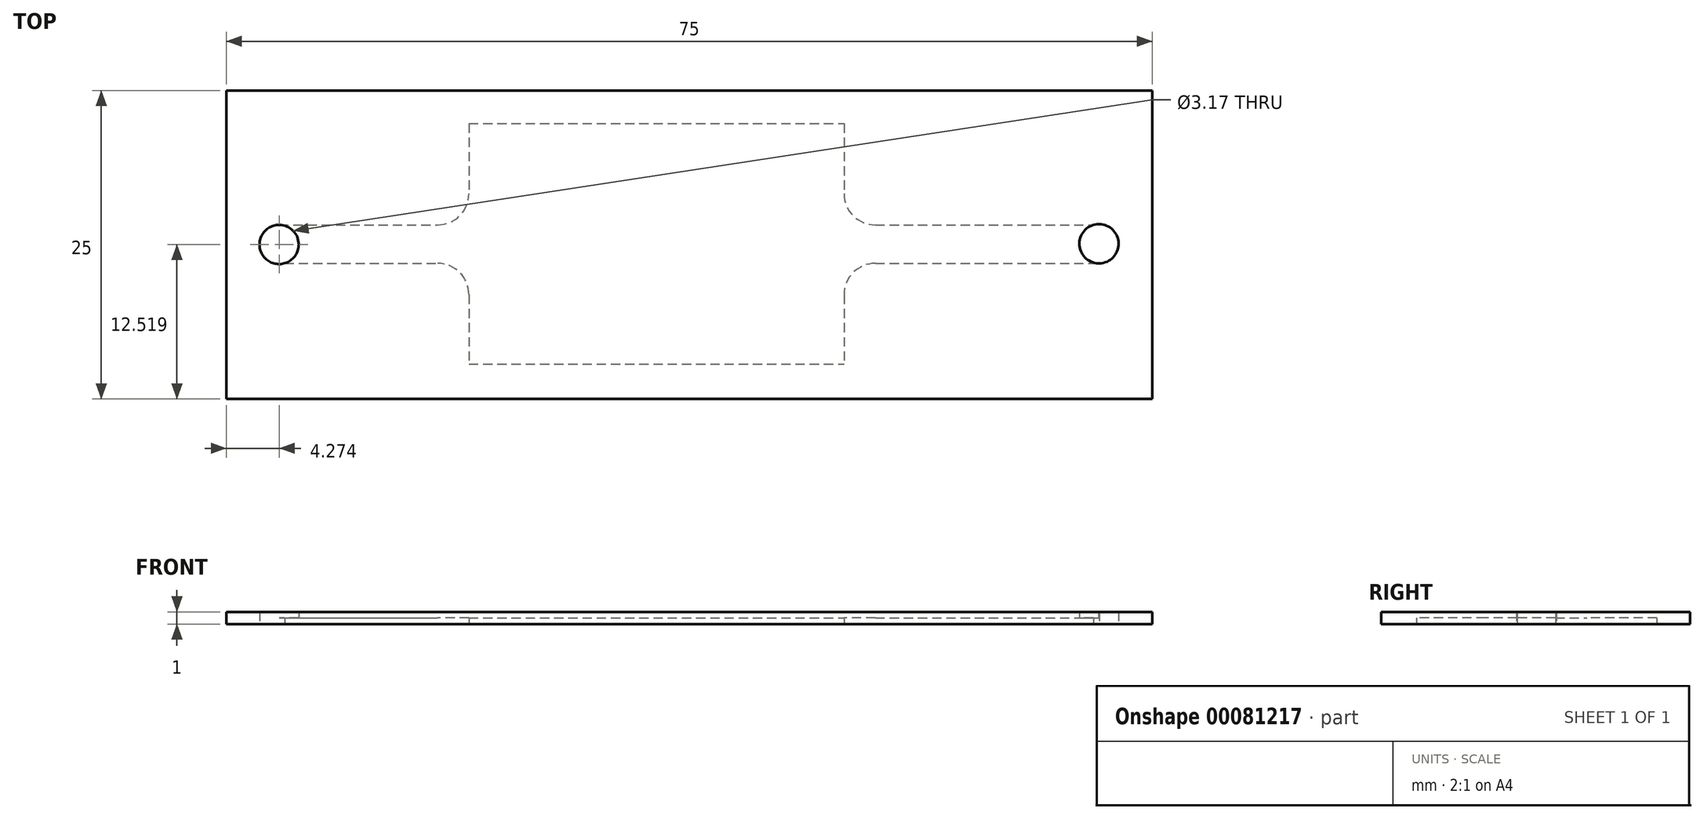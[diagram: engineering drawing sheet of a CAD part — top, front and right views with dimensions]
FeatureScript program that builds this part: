
annotation { "Feature Type Name" : "Feature", "Feature Type Description" : "" }
export const myFeature = defineFeature(function(context is Context, id is Id, definition is map)
    precondition{}
    {
        {
            var Q0;
            Q0=qCreatedBy(makeId("Top.planeOp"),FACE);
            var sketch = newSketch(context, id + "F0", { "sketchPlane" : qUnion([Q0])});
            skLineSegment(sketch, "E0.bottom", {"start": v(40.16, -6.83) * mm, "end": v(-34.84, -6.83) * mm});
            skLineSegment(sketch, "E0.top", {"start": v(40.16, 18.17) * mm, "end": v(-34.84, 18.17) * mm});
            skLineSegment(sketch, "E0.left", {"start": v(40.16, -6.83) * mm, "end": v(40.16, 18.17) * mm});
            skLineSegment(sketch, "E0.right", {"start": v(-34.84, -6.83) * mm, "end": v(-34.84, 18.17) * mm});
            skLineSegment(sketch, "E1", {"start": v(-34.84, -6.83) * mm, "end": v(-34.84, 5.67) * mm});
            skLineSegment(sketch, "E2", {"start": v(-34.84, 5.67) * mm, "end": v(40.16, 5.67) * mm});
            skSolve(sketch);
        }
        {
            var Q0;
            Q0=makeQuery(id+"F0.imprint","IMPRINT",FACE,{"disambiguationData":[TD([[makeQuery(id+"F0.imprint","IMPRINT",EDGE,{"derivedFrom":sQuery(id+"F0.wireOp",EDGE,"E0.bottom")}),-1.0]])]});
            var sketch = newSketch(context, id + "F1", { "sketchPlane" : qUnion([Q0])});
            skCircle(sketch, "E3", {"center": v(35.84, 5.75) * mm, "radius": 1.59 * mm});
            skCircle(sketch, "E4", {"center": v(-30.57, 5.69) * mm, "radius": 1.59 * mm});
            skLineSegment(sketch, "E5.bottom", {"start": v(-30.56, 7.28) * mm, "end": v(35.88, 7.28) * mm});
            skLineSegment(sketch, "E5.top", {"start": v(-30.56, 4.16) * mm, "end": v(35.88, 4.16) * mm});
            skLineSegment(sketch, "E5.left", {"start": v(-30.56, 7.28) * mm, "end": v(-30.56, 4.16) * mm});
            skLineSegment(sketch, "E5.right", {"start": v(35.88, 7.28) * mm, "end": v(35.88, 4.16) * mm});
            skLineSegment(sketch, "E6.bottom", {"start": v(-15.2, 15.49) * mm, "end": v(15.2, 15.49) * mm});
            skLineSegment(sketch, "E6.top", {"start": v(-15.2, -3.99) * mm, "end": v(15.2, -3.99) * mm});
            skLineSegment(sketch, "E6.left", {"start": v(-15.2, 15.49) * mm, "end": v(-15.2, -3.99) * mm});
            skLineSegment(sketch, "E6.right", {"start": v(15.2, 15.49) * mm, "end": v(15.2, -3.99) * mm});
            skPoint(sketch, "E6.middle", {"position": v(0, 5.75) * mm});
            skSolve(sketch);
        }
        {
            var Q0;
            {var subQ0=sQuery(id+"F0.wireOp",EDGE,"E0.bottom");Q0=makeQuery(id+"F0.imprint","IMPRINT",FACE,{"disambiguationData":[TD([[makeQuery(id+"F0.imprint","IMPRINT",EDGE,{"derivedFrom":subQ0}),-1.0]])]});}
            var Q1;
            {var subQ0=sQuery(id+"F0.wireOp",EDGE,"E0.top");Q1=makeQuery(id+"F0.imprint","IMPRINT",FACE,{"disambiguationData":[TD([[makeQuery(id+"F0.imprint","IMPRINT",EDGE,{"derivedFrom":subQ0}),1.0]])]});}
            extrude(context, id + "F2", {"entities" : qUnion([Q0, Q1]), "offsetDistance" : 25.4 * mm, "depth" : 1 * mm});
        }
        {
            var Q0;
            {var subQ1=sQuery(id+"F1.wireOp",EDGE,"E4");var subQ3=makeQuery(id+"F0.imprint","IMPRINT",EDGE,{"derivedFrom":sQuery(id+"F0.wireOp",EDGE,"E2")});var subQ4=makeQuery(id+"F1.imprint","INTERSECT",VERTEX,{"disambiguationData":[OD(0.0)],"derivedFrom":[subQ3,subQ1]});Q0=makeQuery(id+"F1.imprint","IMPRINT",FACE,{"disambiguationData":[TD([[makeQuery(id+"F1.imprint","IMPRINT",EDGE,{"disambiguationData":[TD([[subQ4,-1.0]])],"derivedFrom":subQ3}),1.0]])]});}
            var Q1;
            {var subQ0=sQuery(id+"F1.wireOp",EDGE,"E5.top");var subQ1=sQuery(id+"F1.wireOp",EDGE,"E4");var subQ2=makeQuery(id+"F1.imprint","INTERSECT",VERTEX,{"derivedFrom":[subQ1,subQ0]});Q1=makeQuery(id+"F1.imprint","IMPRINT",FACE,{"disambiguationData":[TD([[makeQuery(id+"F1.imprint","IMPRINT",EDGE,{"disambiguationData":[TD([[subQ2,1.0]])],"derivedFrom":subQ1}),1.0]])]});}
            var Q2;
            {var subQ0=sQuery(id+"F1.wireOp",EDGE,"E5.top");var subQ1=sQuery(id+"F1.wireOp",EDGE,"E4");var subQ2=makeQuery(id+"F1.imprint","INTERSECT",VERTEX,{"derivedFrom":[subQ1,subQ0]});Q2=makeQuery(id+"F1.imprint","IMPRINT",FACE,{"disambiguationData":[TD([[makeQuery(id+"F1.imprint","IMPRINT",EDGE,{"disambiguationData":[TD([[subQ2,-1.0]])],"derivedFrom":subQ1}),1.0]])]});}
            var Q3;
            {var subQ0=sQuery(id+"F1.wireOp",EDGE,"e85cab8e-166c-4b5d-8382-3d215b1240e5");var subQ1=sQuery(id+"F1.wireOp",EDGE,"E4");var subQ2=makeQuery(id+"F1.imprint","INTERSECT",VERTEX,{"derivedFrom":[subQ1,subQ0]});Q3=makeQuery(id+"F1.imprint","IMPRINT",FACE,{"disambiguationData":[TD([[makeQuery(id+"F1.imprint","IMPRINT",EDGE,{"disambiguationData":[TD([[subQ2,1.0]])],"derivedFrom":subQ1}),1.0]])]});}
            var Q4;
            {var subQ0=sQuery(id+"F1.wireOp",EDGE,"E5.bottom");var subQ1=sQuery(id+"F1.wireOp",EDGE,"E3");var subQ2=makeQuery(id+"F1.imprint","INTERSECT",VERTEX,{"derivedFrom":[subQ1,subQ0]});Q4=makeQuery(id+"F1.imprint","IMPRINT",FACE,{"disambiguationData":[TD([[makeQuery(id+"F1.imprint","IMPRINT",EDGE,{"disambiguationData":[TD([[subQ2,-1.0]])],"derivedFrom":subQ1}),1.0]])]});}
            var Q5;
            {var subQ0=sQuery(id+"F1.wireOp",EDGE,"E5.top");var subQ1=sQuery(id+"F1.wireOp",EDGE,"E3");var subQ2=makeQuery(id+"F1.imprint","INTERSECT",VERTEX,{"derivedFrom":[subQ1,subQ0]});Q5=makeQuery(id+"F1.imprint","IMPRINT",FACE,{"disambiguationData":[TD([[makeQuery(id+"F1.imprint","IMPRINT",EDGE,{"disambiguationData":[TD([[subQ2,1.0]])],"derivedFrom":subQ1}),1.0]])]});}
            var Q6;
            {var subQ1=sQuery(id+"F1.wireOp",EDGE,"E3");var subQ3=makeQuery(id+"F0.imprint","IMPRINT",EDGE,{"derivedFrom":sQuery(id+"F0.wireOp",EDGE,"E2")});var subQ4=makeQuery(id+"F1.imprint","INTERSECT",VERTEX,{"disambiguationData":[OD(0.0)],"derivedFrom":[subQ3,subQ1]});Q6=makeQuery(id+"F1.imprint","IMPRINT",FACE,{"disambiguationData":[TD([[makeQuery(id+"F1.imprint","IMPRINT",EDGE,{"disambiguationData":[TD([[subQ4,1.0]])],"derivedFrom":subQ3}),-1.0]])]});}
            var Q7;
            {var subQ0=sQuery(id+"F1.wireOp",EDGE,"E5.bottom");var subQ1=sQuery(id+"F1.wireOp",EDGE,"E3");var subQ2=makeQuery(id+"F1.imprint","INTERSECT",VERTEX,{"derivedFrom":[subQ1,subQ0]});Q7=makeQuery(id+"F1.imprint","IMPRINT",FACE,{"disambiguationData":[TD([[makeQuery(id+"F1.imprint","IMPRINT",EDGE,{"disambiguationData":[TD([[subQ2,1.0]])],"derivedFrom":subQ1}),1.0]])]});}
            var Q8;
            {var subQ1=sQuery(id+"F1.wireOp",EDGE,"E4");var subQ3=makeQuery(id+"F0.imprint","IMPRINT",EDGE,{"derivedFrom":sQuery(id+"F0.wireOp",EDGE,"E2")});var subQ4=makeQuery(id+"F1.imprint","INTERSECT",VERTEX,{"disambiguationData":[OD(1.0)],"derivedFrom":[subQ3,subQ1]});Q8=makeQuery(id+"F1.imprint","IMPRINT",FACE,{"disambiguationData":[TD([[makeQuery(id+"F1.imprint","IMPRINT",EDGE,{"disambiguationData":[TD([[subQ4,1.0]])],"derivedFrom":subQ3}),1.0]])]});}
            extrude(context, id + "F3", {"entities" : qUnion([Q0, Q1, Q2, Q3, Q4, Q5, Q6, Q7, Q8]), "operationType" : NewBodyOperationType.REMOVE, "depth" : 25.4 * mm});
        }
        {
            var Q0;
            {var subQ1=sQuery(id+"F1.wireOp",EDGE,"E5.top");var subQ8=sQuery(id+"F1.wireOp",EDGE,"E4");var subQ9=makeQuery(id+"F1.imprint","INTERSECT",VERTEX,{"derivedFrom":[subQ8,subQ1]});Q0=makeQuery(id+"F1.imprint","IMPRINT",FACE,{"disambiguationData":[TD([[makeQuery(id+"F1.imprint","IMPRINT",EDGE,{"disambiguationData":[TD([[subQ9,-1.0]])],"derivedFrom":subQ8}),-1.0]])]});}
            var Q1;
            {var subQ0=sQuery(id+"F1.wireOp",EDGE,"e85cab8e-166c-4b5d-8382-3d215b1240e5");var subQ3=sQuery(id+"F1.wireOp",EDGE,"E4");var subQ4=makeQuery(id+"F1.imprint","INTERSECT",VERTEX,{"derivedFrom":[subQ3,subQ0]});Q1=makeQuery(id+"F1.imprint","IMPRINT",FACE,{"disambiguationData":[TD([[makeQuery(id+"F1.imprint","IMPRINT",EDGE,{"disambiguationData":[TD([[subQ4,1.0]])],"derivedFrom":subQ3}),-1.0]])]});}
            var Q2;
            {var subQ5=sQuery(id+"F1.wireOp",EDGE,"E6.top");Q2=makeQuery(id+"F1.imprint","IMPRINT",FACE,{"disambiguationData":[TD([[makeQuery(id+"F1.imprint","IMPRINT",EDGE,{"derivedFrom":subQ5}),1.0]])]});}
            var Q3;
            {var subQ5=sQuery(id+"F1.wireOp",EDGE,"E6.bottom");Q3=makeQuery(id+"F1.imprint","IMPRINT",FACE,{"disambiguationData":[TD([[makeQuery(id+"F1.imprint","IMPRINT",EDGE,{"derivedFrom":subQ5}),-1.0]])]});}
            var Q4;
            {var subQ1=sQuery(id+"F1.wireOp",EDGE,"E5.bottom");var subQ7=sQuery(id+"F1.wireOp",EDGE,"E3");var subQ8=makeQuery(id+"F1.imprint","INTERSECT",VERTEX,{"derivedFrom":[subQ7,subQ1]});Q4=makeQuery(id+"F1.imprint","IMPRINT",FACE,{"disambiguationData":[TD([[makeQuery(id+"F1.imprint","IMPRINT",EDGE,{"disambiguationData":[TD([[subQ8,-1.0]])],"derivedFrom":subQ7}),-1.0]])]});}
            var Q5;
            {var subQ1=sQuery(id+"F1.wireOp",EDGE,"E5.top");var subQ3=sQuery(id+"F1.wireOp",EDGE,"E3");var subQ4=makeQuery(id+"F1.imprint","INTERSECT",VERTEX,{"derivedFrom":[subQ3,subQ1]});Q5=makeQuery(id+"F1.imprint","IMPRINT",FACE,{"disambiguationData":[TD([[makeQuery(id+"F1.imprint","IMPRINT",EDGE,{"disambiguationData":[TD([[subQ4,1.0]])],"derivedFrom":subQ3}),-1.0]])]});}
            var Q6;
            {var subQ0=sQuery(id+"F1.wireOp",EDGE,"E6.left");var subQ1=sQuery(id+"F1.wireOp",EDGE,"E5.bottom");var subQ2=makeQuery(id+"F1.imprint","INTERSECT",VERTEX,{"derivedFrom":[subQ1,subQ0]});Q6=makeQuery(id+"F1.imprint","IMPRINT",FACE,{"disambiguationData":[TD([[makeQuery(id+"F1.imprint","IMPRINT",EDGE,{"disambiguationData":[TD([[subQ2,-1.0]])],"derivedFrom":subQ1}),-1.0]])]});}
            var Q7;
            {var subQ0=sQuery(id+"F1.wireOp",EDGE,"E6.left");var subQ1=sQuery(id+"F1.wireOp",EDGE,"E5.top");var subQ2=makeQuery(id+"F1.imprint","INTERSECT",VERTEX,{"derivedFrom":[subQ1,subQ0]});Q7=makeQuery(id+"F1.imprint","IMPRINT",FACE,{"disambiguationData":[TD([[makeQuery(id+"F1.imprint","IMPRINT",EDGE,{"disambiguationData":[TD([[subQ2,-1.0]])],"derivedFrom":subQ1}),1.0]])]});}
            var Q8;
            {var subQ0=sQuery(id+"F1.wireOp",EDGE,"f7442fb1-22eb-4b81-94ff-7a8b5c8a4ed30.MirrorCS");var subQ1=sQuery(id+"F1.wireOp",EDGE,"E5.top");var subQ2=makeQuery(id+"F1.imprint","INTERSECT",VERTEX,{"disambiguationData":[OD(0.0)],"derivedFrom":[subQ1,subQ0]});Q8=makeQuery(id+"F1.imprint","IMPRINT",FACE,{"disambiguationData":[TD([[makeQuery(id+"F1.imprint","IMPRINT",EDGE,{"disambiguationData":[TD([[subQ2,-1.0]])],"derivedFrom":subQ1}),1.0]])]});}
            var Q9;
            {var subQ0=sQuery(id+"F1.wireOp",EDGE,"9eba685b-acd6-4631-9a7d-23c258058f2e0.MirrorCS");var subQ1=sQuery(id+"F1.wireOp",EDGE,"E5.top");var subQ2=makeQuery(id+"F1.imprint","INTERSECT",VERTEX,{"disambiguationData":[OD(0.0)],"derivedFrom":[subQ1,subQ0]});Q9=makeQuery(id+"F1.imprint","IMPRINT",FACE,{"disambiguationData":[TD([[makeQuery(id+"F1.imprint","IMPRINT",EDGE,{"disambiguationData":[TD([[subQ2,-1.0]])],"derivedFrom":subQ1}),1.0]])]});}
            var Q10;
            {var subQ0=sQuery(id+"F1.wireOp",EDGE,"c3d708f8-f24b-45cc-bd9d-1248575bf3a40.MirrorCS");var subQ1=sQuery(id+"F1.wireOp",EDGE,"E5.bottom");var subQ2=makeQuery(id+"F1.imprint","INTERSECT",VERTEX,{"disambiguationData":[OD(0.0)],"derivedFrom":[subQ1,subQ0]});Q10=makeQuery(id+"F1.imprint","IMPRINT",FACE,{"disambiguationData":[TD([[makeQuery(id+"F1.imprint","IMPRINT",EDGE,{"disambiguationData":[TD([[subQ2,1.0]])],"derivedFrom":subQ1}),-1.0]])]});}
            extrude(context, id + "F4", {"entities" : qUnion([Q0, Q1, Q2, Q3, Q4, Q5, Q6, Q7, Q8, Q9, Q10]), "operationType" : NewBodyOperationType.REMOVE, "offsetDistance" : 25 * mm, "depth" : 0.5 * mm});
        }
        {
            var Q0;
            Q0=makeQuery(id+"F4.boolean.opBoolean","COPY",EDGE,{"derivedFrom":makeQuery(id+"F4.opExtrude","SWEPT_EDGE",EDGE,{"disambiguationData":[OSD([sQuery(id+"F1.wireOp",EDGE,"E5.top"),sQuery(id+"F1.wireOp",EDGE,"E6.left")])]})});
            var Q1;
            Q1=makeQuery(id+"F4.boolean.opBoolean","COPY",EDGE,{"derivedFrom":makeQuery(id+"F4.opExtrude","SWEPT_EDGE",EDGE,{"disambiguationData":[OSD([sQuery(id+"F1.wireOp",EDGE,"E5.bottom"),sQuery(id+"F1.wireOp",EDGE,"E6.left")])]})});
            var Q2;
            Q2=makeQuery(id+"F4.boolean.opBoolean","COPY",EDGE,{"derivedFrom":makeQuery(id+"F4.opExtrude","SWEPT_EDGE",EDGE,{"disambiguationData":[OSD([sQuery(id+"F1.wireOp",EDGE,"E5.top"),sQuery(id+"F1.wireOp",EDGE,"E6.right")])]})});
            var Q3;
            Q3=makeQuery(id+"F4.boolean.opBoolean","COPY",EDGE,{"derivedFrom":makeQuery(id+"F4.opExtrude","SWEPT_EDGE",EDGE,{"disambiguationData":[OSD([sQuery(id+"F1.wireOp",EDGE,"E5.bottom"),sQuery(id+"F1.wireOp",EDGE,"E6.right")])]})});
            fillet(context, id + "F5", {"entities" : qUnion([Q0, Q1, Q2, Q3]), "radius" : 2.54 * mm, "tangentPropagation" : true, "allowEdgeOverflow" : false});
        }
    });
